# Revit family: Diffuser-Carnes-SPRB-Round_Neck
name_source: partatom
category: Duct Accessories
revit_build: Autodesk Revit Architecture 2012 (Build: 20110309_2315(x64)
units: mm (PartAtom-declared; Revit-internal decimal feet)

## types (13) — shared parameters
Catalog = http://www.carnes.com
Default Elevation = 0"
Description = Perforated Diffusers
Diameter = 4.00"
Diffuser Plate = Metal - Carnes - Plate - Mesh
Flow = 0 CFM
Manufacturer = CARNES COMPANY
Model = SPRB
Panel Options = http://www.carnes.com
Product Page URL = http://www.carnes.com
Radius = 2.00"
Return Connection = Diffuser Return Connector
Return Connector = Yes
Specification Sheet = http://www.carnes.com
Subcatagory = Air Distribution
URL = http://www.carnes.com
Unit = Metal - Carnes - Steel Galvanized

## per-type parameters (varying)
| type | Height C | Width A |
| SPRB 114x5 | 2 1/2" | 11 3/4" |
| SPRB 114x6 | 2 1/2" | 11 3/4" |
| SPRB 114x7 | 2 1/2" | 11 3/4" |
| SPRB 114x8 | 2 1/2" | 11 3/4" |
| SPRB 224x5 | 2 3/4" | 23 3/4" |
| SPRB 224x6 | 2 3/4" | 23 3/4" |
| SPRB 224x7 | 2 3/4" | 23 3/4" |
| SPRB 224x8 | 2 3/4" | 23 3/4" |
| SPRB 224x10 | 2 3/4" | 23 3/4" |
| SPRB 224x12 | 2 3/4" | 23 3/4" |
| SPRB 224x14 | 2 3/4" | 23 3/4" |
| SPRB 224x16 | 2 3/4" | 23 3/4" |
| SPRB 224x18 | 2 3/4" | 23 3/4" |

## geometry (parser evidence)
native form markers: Blend x6, Sweep x3
no freeform markers — native parametric forms only
